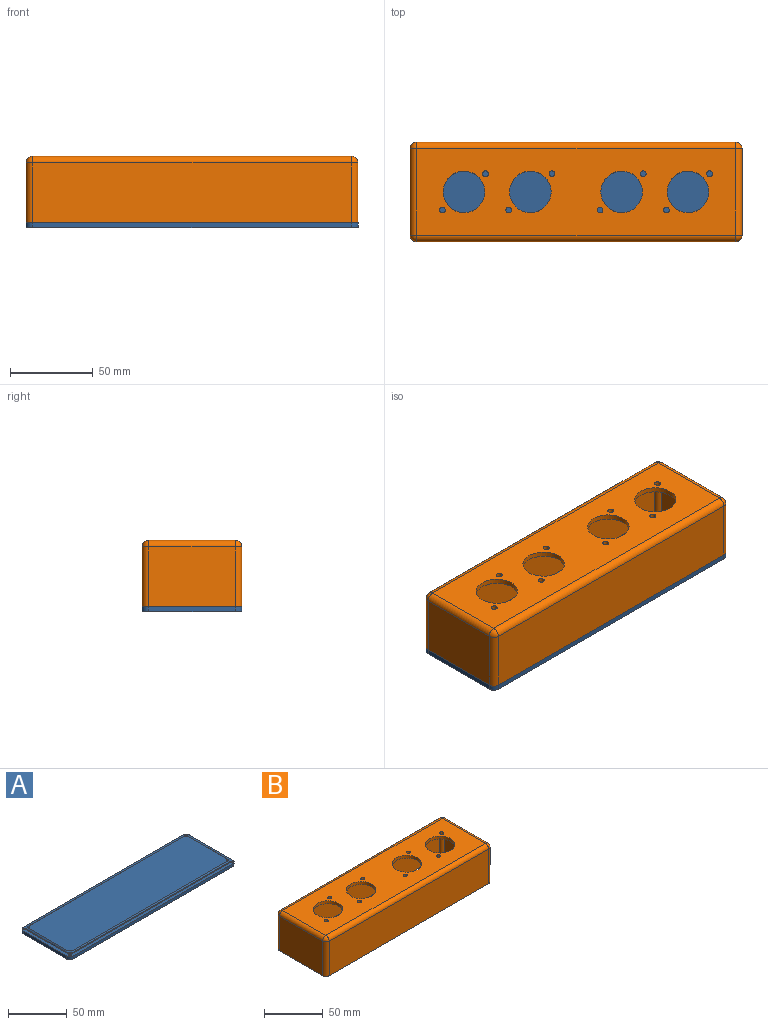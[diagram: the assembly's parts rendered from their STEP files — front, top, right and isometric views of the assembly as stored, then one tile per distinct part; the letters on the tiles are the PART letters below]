
ASSEMBLY  parts=2 mates=1
PART A: 35 faces, bbox 200.1x60.1x5.1 mm
  f0: plane 200x60mm, normal (0,0,1), area 1518.9mm2, adj f1,f2,f3,f4,f6,f7,f8,f9
  f1: plane 192x3mm, normal (0,-1,0), area 576mm2, adj f0,f5,f31,f32
  f2: plane 52x3mm, normal (1,0,0), area 156mm2, adj f0,f5,f32,f33
  f3: plane 192x3mm, normal (0,1,0), area 576mm2, adj f0,f5,f33,f34
  f4: plane 52x3mm, normal (-1,0,0), area 156mm2, adj f0,f5,f31,f34
  f5: plane 200x60mm, normal (0,0,-1), area 11933.5mm2, adj f1,f2,f3,f4,f27,f28,f29,f30
  f6: cylinder r=3mm len=3mm, axis (0,0,1), area 4.7mm2, adj f0,f7,f13,f19
  f7: plane 48x1mm, normal (1,0,0), area 48mm2, adj f0,f6,f8,f21
  f8: cylinder r=3mm len=3mm, axis (0,0,1), area 4.7mm2, adj f0,f7,f9,f22
  f9: plane 188x1mm, normal (0,1,0), area 188mm2, adj f0,f8,f10,f20
  f10: cylinder r=3mm len=3mm, axis (0,0,1), area 4.7mm2, adj f0,f9,f11,f18
  f11: plane 48x1mm, normal (-1,0,0), area 48mm2, adj f0,f10,f12,f16
  f12: cylinder r=3mm len=3mm, axis (0,0,1), area 4.7mm2, adj f0,f11,f13,f15
  f13: plane 188x1mm, normal (0,-1,0), area 188mm2, adj f0,f6,f12,f17
  f14: plane 192x52mm, normal (0,0,1), area 9961.4mm2, adj f15,f16,f17,f18,f19,f20,f21,f22
  f15: cone r=3mm half-angle=45deg, axis (0,0,1), area 6.5mm2, adj f12,f14,f16,f17
  f16: plane 48.11x1.11mm, normal (-0.71,0,0.71), area 66.6mm2, adj f11,f14,f15,f18
  f17: plane 188.11x1.11mm, normal (0,-0.71,0.71), area 264.6mm2, adj f13,f14,f15,f19
  f18: cone r=3mm half-angle=45deg, axis (0,0,1), area 6.5mm2, adj f10,f14,f16,f20
  f19: cone r=3mm half-angle=45deg, axis (0,0,1), area 6.5mm2, adj f6,f14,f17,f21
  f20: plane 188.11x1.11mm, normal (0,0.71,0.71), area 264.6mm2, adj f9,f14,f18,f22
  f21: plane 48.11x1.11mm, normal (0.71,0,0.71), area 66.6mm2, adj f7,f14,f19,f22
  f22: cone r=3mm half-angle=45deg, axis (0,0,1), area 6.5mm2, adj f8,f14,f20,f21
  f23: cylinder r=1.25mm len=2.5mm, axis (0,0,-1), area 17.3mm2, adj f0,f27
  f24: cylinder r=1.25mm len=2.5mm, axis (0,0,-1), area 17.3mm2, adj f0,f28
  f25: cylinder r=1.25mm len=2.5mm, axis (0,0,-1), area 17.3mm2, adj f0,f29
  f26: cylinder r=1.25mm len=2.5mm, axis (0,0,-1), area 17.3mm2, adj f0,f30
  f27: cone r=1.25mm half-angle=45deg, axis (0,0,-1), area 11.7mm2, adj f5,f23
  f28: cone r=1.25mm half-angle=45deg, axis (0,0,-1), area 11.7mm2, adj f5,f24
  f29: cone r=1.25mm half-angle=45deg, axis (0,0,-1), area 11.7mm2, adj f5,f25
  f30: cone r=1.25mm half-angle=45deg, axis (0,0,-1), area 11.7mm2, adj f5,f26
  f31: cylinder r=4mm len=4mm, axis (0,0,1), area 18.8mm2, adj f0,f1,f4,f5
  f32: cylinder r=4mm len=4mm, axis (0,0,-1), area 18.8mm2, adj f0,f1,f2,f5
  f33: cylinder r=4mm len=4mm, axis (0,0,1), area 18.8mm2, adj f0,f2,f3,f5
  f34: cylinder r=4mm len=4mm, axis (0,0,-1), area 18.8mm2, adj f0,f3,f4,f5
PART B: 59 faces, bbox 200x60x40 mm
  f0: plane 192x36mm, normal (0,-1,0), area 6912mm2, adj f5,f20,f24,f26
  f1: plane 52x36mm, normal (1,0,0), area 1872mm2, adj f5,f15,f19,f20
  f2: plane 192x36mm, normal (0,1,0), area 6907.2mm2, adj f5,f15,f17,f18,f55,f56,f57,f58
  f3: plane 52x36mm, normal (-1,0,0), area 1872mm2, adj f5,f17,f23,f26
  f4: plane 192x52mm, normal (0,0,1), area 7943.5mm2, adj f18,f19,f23,f24,f43,f44,f45,f46
  f5: plane 200x60mm, normal (0,0,-1), area 1022.5mm2, adj f0,f1,f2,f3,f15,f17,f20,f26
  f6: cylinder r=3mm len=36mm, axis (0,0,-1), area 169.6mm2, adj f7,f13,f14,f38
  f7: plane 48x36mm, normal (-1,0,0), area 1728mm2, adj f6,f8,f14,f36
  f8: cylinder r=3mm len=36mm, axis (0,0,-1), area 169.6mm2, adj f7,f9,f14,f35
  f9: plane 188x36mm, normal (0,1,0), area 6768mm2, adj f8,f10,f14,f37
  f10: cylinder r=3mm len=36mm, axis (0,0,-1), area 169.6mm2, adj f9,f11,f14,f39
  f11: plane 48x36mm, normal (1,0,0), area 1728mm2, adj f10,f12,f14,f41
  f12: cylinder r=3mm len=36mm, axis (0,0,-1), area 169.6mm2, adj f11,f13,f14,f42
  f13: plane 188x36mm, normal (0,-1,0), area 6763.2mm2, adj f6,f12,f14,f40,f55,f56,f57,f58
  f14: plane 194x54mm, normal (0,0,-1), area 8407.3mm2, adj f6,f7,f8,f9,f10,f11,f12,f13
  f15: cylinder r=4mm len=36mm, axis (0,0,1), area 226.2mm2, adj f1,f2,f5,f16
  f16: sphere r=4mm, area 25.1mm2, adj f15,f18,f19
  f17: cylinder r=4mm len=36mm, axis (0,0,-1), area 226.2mm2, adj f2,f3,f5,f21
  f18: cylinder r=4mm len=192mm, axis (-1,0,0), area 1206.4mm2, adj f2,f4,f16,f21
  f19: cylinder r=4mm len=52mm, axis (0,1,0), area 326.7mm2, adj f1,f4,f16,f22
  f20: cylinder r=4mm len=36mm, axis (0,0,-1), area 226.2mm2, adj f0,f1,f5,f22
  f21: sphere r=4mm, area 25.1mm2, adj f17,f18,f23
  f22: sphere r=4mm, area 25.1mm2, adj f19,f20,f24
  f23: cylinder r=4mm len=52mm, axis (0,-1,0), area 326.7mm2, adj f3,f4,f21,f25
  f24: cylinder r=4mm len=192mm, axis (1,0,0), area 1206.4mm2, adj f0,f4,f22,f25
  f25: sphere r=4mm, area 25.1mm2, adj f23,f24,f26
  f26: cylinder r=4mm len=36mm, axis (0,0,1), area 226.2mm2, adj f0,f3,f5,f25
  f27: cylinder r=1.25mm len=10mm, axis (0,0,-1), area 78.5mm2, adj f5,f28
  f28: plane 2.5x2.5mm, normal (0,0,-1), area 4.9mm2, adj f27
  f29: cylinder r=1.25mm len=10mm, axis (0,0,-1), area 78.5mm2, adj f5,f30
  f30: plane 2.5x2.5mm, normal (0,0,-1), area 4.9mm2, adj f29
  f31: cylinder r=1.25mm len=10mm, axis (0,0,-1), area 78.5mm2, adj f5,f32
  f32: plane 2.5x2.5mm, normal (0,0,-1), area 4.9mm2, adj f31
  f33: cylinder r=1.25mm len=10mm, axis (0,0,-1), area 78.5mm2, adj f5,f34
  f34: plane 2.5x2.5mm, normal (0,0,-1), area 4.9mm2, adj f33
  f35: cone r=2mm half-angle=45deg, axis (0,0,1), area 7mm2, adj f5,f8,f36,f37
  f36: plane 50.54x1mm, normal (-0.71,0,-0.71), area 69.5mm2, adj f5,f7,f35,f38
  f37: plane 190.54x1mm, normal (0,0.71,-0.71), area 267.5mm2, adj f5,f9,f35,f39
  f38: cone r=2mm half-angle=45deg, axis (0,0,1), area 7mm2, adj f5,f6,f36,f40
  f39: cone r=2mm half-angle=45deg, axis (0,0,1), area 7mm2, adj f5,f10,f37,f41
  f40: plane 190.54x1mm, normal (0,-0.71,-0.71), area 267.5mm2, adj f5,f13,f38,f42
  f41: plane 50.54x1mm, normal (0.71,0,-0.71), area 69.5mm2, adj f5,f11,f39,f42
  f42: cone r=2mm half-angle=45deg, axis (0,0,1), area 7mm2, adj f5,f12,f40,f41
  f43: cylinder r=1.75mm len=3.5mm, axis (0,0,1), area 33mm2, adj f4,f14
  f44: cylinder r=12.5mm len=25mm, axis (0,0,1), area 235.6mm2, adj f4,f14
  f45: cylinder r=1.75mm len=3.5mm, axis (0,0,1), area 33mm2, adj f4,f14
  f46: cylinder r=1.75mm len=3.5mm, axis (0,0,1), area 33mm2, adj f4,f14
  f47: cylinder r=1.75mm len=3.5mm, axis (0,0,1), area 33mm2, adj f4,f14
  f48: cylinder r=12.5mm len=25mm, axis (0,0,1), area 235.6mm2, adj f4,f14
  f49: cylinder r=1.75mm len=3.5mm, axis (0,0,1), area 33mm2, adj f4,f14
  f50: cylinder r=12.5mm len=25mm, axis (0,0,1), area 235.6mm2, adj f4,f14
  f51: cylinder r=1.75mm len=3.5mm, axis (0,0,1), area 33mm2, adj f4,f14
  f52: cylinder r=12.5mm len=25mm, axis (0,0,1), area 235.6mm2, adj f4,f14
  f53: cylinder r=1.75mm len=3.5mm, axis (0,0,1), area 33mm2, adj f4,f14
  f54: cylinder r=1.75mm len=3.5mm, axis (0,0,1), area 33mm2, adj f4,f14
  f55: plane 3x2mm, normal (0,0,-1), area 6mm2, adj f2,f13,f56,f58
  f56: cylinder r=0.75mm len=3mm, axis (0,1,0), area 7.1mm2, adj f2,f13,f55,f57
  f57: plane 3x2mm, normal (0,0,1), area 6mm2, adj f2,f13,f56,f58
  f58: cylinder r=0.75mm len=3mm, axis (0,1,0), area 7.1mm2, adj f2,f13,f55,f57
PLACE A t=(4.17,5.73,-18.02)mm
PLACE B t=(4.17,5.73,-15.02)mm
MATE fastened A.f0 <-> B.f5  axis (0,0,1) through (4.17,5.73,-15.02)mm
